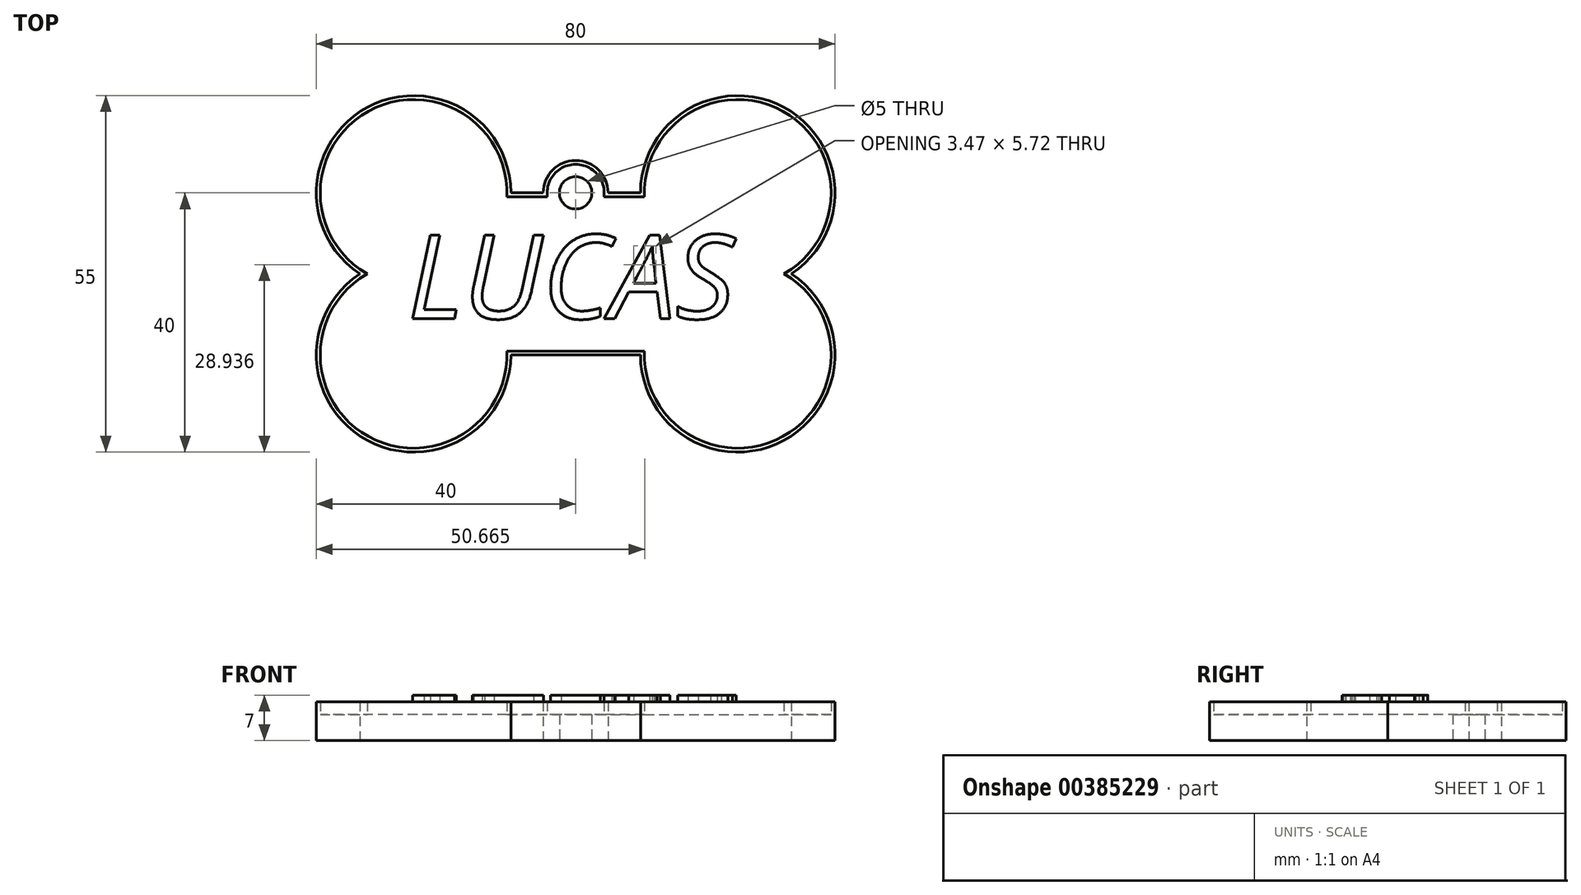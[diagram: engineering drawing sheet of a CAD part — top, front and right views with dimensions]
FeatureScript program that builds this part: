
annotation { "Feature Type Name" : "Feature", "Feature Type Description" : "" }
export const myFeature = defineFeature(function(context is Context, id is Id, definition is map)
    precondition{}
    {
        {
            var Q0;
            Q0=qCreatedBy(makeId("Top.planeOp"),FACE);
            var sketch = newSketch(context, id + "F0", { "sketchPlane" : qUnion([Q0])});
            skLineSegment(sketch, "E0.bottom", {"start": v(-10, 12.5) * mm, "end": v(-5, 12.5) * mm});
            skLineSegment(sketch, "E0.top", {"start": v(-10, -12.5) * mm, "end": v(10, -12.5) * mm});
            skArc(sketch, "E1", {"start": v(-10, 12.5) * mm, "mid": v(-32.1, 25.72) * mm, "end": v(-33.3, 0) * mm});
            skArc(sketch, "E2", {"start": v(33.3, 0) * mm, "mid": v(32.1, 25.72) * mm, "end": v(10, 12.5) * mm});
            skArc(sketch, "E3", {"start": v(-33.3, 0) * mm, "mid": v(-32.1, -25.72) * mm, "end": v(-10, -12.5) * mm});
            skArc(sketch, "E4", {"start": v(10, -12.5) * mm, "mid": v(32.1, -25.72) * mm, "end": v(33.3, 0) * mm});
            skArc(sketch, "E5", {"start": v(5, 12.5) * mm, "mid": v(0, 17.5) * mm, "end": v(-5, 12.5) * mm});
            skLineSegment(sketch, "E6.trimOffspring", {"start": v(5, 12.5) * mm, "end": v(10, 12.5) * mm});
            skCircle(sketch, "E7", {"center": v(0, 12.5) * mm, "radius": 2.5 * mm});
            skSolve(sketch);
        }
        {
            var Q0;
            Q0 = qSketchRegion(id + "F0", true);
            extrude(context, id + "F1", {"entities" : qUnion([Q0]), "depth" : 4 * mm});
        }
        {
            var Q0;
            Q0=makeQuery(id+"F1.opExtrude","CAP_FACE",FACE,{"disambiguationData":[OSD([sQuery(id+"F0.wireOp",EDGE,"E0.bottom"),sQuery(id+"F0.wireOp",EDGE,"E0.top"),sQuery(id+"F0.wireOp",EDGE,"E1"),sQuery(id+"F0.wireOp",EDGE,"E2"),sQuery(id+"F0.wireOp",EDGE,"E3"),sQuery(id+"F0.wireOp",EDGE,"E4"),sQuery(id+"F0.wireOp",EDGE,"E5"),sQuery(id+"F0.wireOp",EDGE,"E6.trimOffspring"),sQuery(id+"F0.wireOp",EDGE,"E7")])],"isStart":false});
            var sketch = newSketch(context, id + "F2", { "sketchPlane" : qUnion([Q0])});
            skArc(sketch, "E8.0", {"start": v(-32.15, 0) * mm, "mid": v(-31.96, -25.1) * mm, "end": v(-10.61, -11.9) * mm});
            skArc(sketch, "E8.1", {"start": v(-10.61, 11.9) * mm, "mid": v(-31.96, 25.1) * mm, "end": v(-32.15, 0) * mm});
            skLineSegment(sketch, "E8.2", {"start": v(-10.61, -11.9) * mm, "end": v(10.61, -11.9) * mm});
            skLineSegment(sketch, "E8.3", {"start": v(-4.36, 11.9) * mm, "end": v(-10.61, 11.9) * mm});
            skArc(sketch, "E8.4", {"start": v(10.61, -11.9) * mm, "mid": v(31.96, -25.1) * mm, "end": v(32.15, 0) * mm});
            skArc(sketch, "E8.5", {"start": v(32.15, 0) * mm, "mid": v(31.96, 25.1) * mm, "end": v(10.61, 11.9) * mm});
            skLineSegment(sketch, "E8.6", {"start": v(10.61, 11.9) * mm, "end": v(4.36, 11.9) * mm});
            skArc(sketch, "E8.7", {"start": v(4.36, 11.9) * mm, "mid": v(0, 16.9) * mm, "end": v(-4.36, 11.9) * mm});
            skSolve(sketch);
        }
        {
            var Q0;
            Q0=makeQuery(id+"F2.imprint","IMPRINT",FACE,{"disambiguationData":[TD([[makeQuery(id+"F2.imprint","IMPRINT",EDGE,{"derivedFrom":sQuery(id+"F2.wireOp",EDGE,"E8.0")}),-1.0]])]});
            extrude(context, id + "F3", {"entities" : qUnion([Q0]), "operationType" : NewBodyOperationType.ADD, "depth" : 2 * mm});
        }
        {
            var Q0;
            Q0=makeQuery(id+"F3.opExtrude","CAP_FACE",FACE,{"disambiguationData":[OSD([sQuery(id+"F0.wireOp",EDGE,"E0.bottom"),sQuery(id+"F0.wireOp",EDGE,"E0.top"),sQuery(id+"F0.wireOp",EDGE,"E1"),sQuery(id+"F0.wireOp",EDGE,"E2"),sQuery(id+"F0.wireOp",EDGE,"E3"),sQuery(id+"F0.wireOp",EDGE,"E4"),sQuery(id+"F0.wireOp",EDGE,"E5"),sQuery(id+"F0.wireOp",EDGE,"E6.trimOffspring"),sQuery(id+"F2.wireOp",EDGE,"E8.0"),sQuery(id+"F2.wireOp",EDGE,"E8.1"),sQuery(id+"F2.wireOp",EDGE,"E8.2"),sQuery(id+"F2.wireOp",EDGE,"E8.3"),sQuery(id+"F2.wireOp",EDGE,"E8.4"),sQuery(id+"F2.wireOp",EDGE,"E8.5"),sQuery(id+"F2.wireOp",EDGE,"E8.6"),sQuery(id+"F2.wireOp",EDGE,"E8.7")])],"isStart":false});
            var sketch = newSketch(context, id + "F4", { "sketchPlane" : qUnion([Q0])});
            skText(sketch, "E9", { "text": "LUCAS", "fontName": "OpenSans-Italic.ttf"});
            const initialGuessF4  = {"E9": [-0.02593, -0.0069, 1, 0, 0.013]};
            skSetInitialGuess(sketch, initialGuessF4);
            skSolve(sketch);
        }
        {
            var Q0;
            Q0 = qSketchRegion(id + "F4", true);
            extrude(context, id + "F5", {"entities" : qUnion([Q0]), "depth" : 1 * mm});
        }
    });
